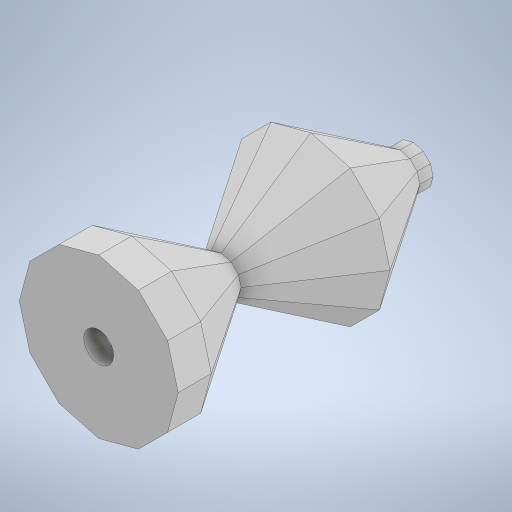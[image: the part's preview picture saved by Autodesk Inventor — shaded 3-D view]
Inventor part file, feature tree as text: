
AUTODESK INVENTOR PART (.ipt)
format: ipt  version: 2023 (Build 270158000, 158)  size: 357,376 bytes
history: native  units: in
note: dims shown in document units (in); Inventor stores cm internally (conversion verified against a paired STEP export)
features: sketch x7, extrude x4, projected_geometry x3, other x2, mirror x2, loft x1, shell x1
ambient origin geometry x8: Origin, YZ Plane, XZ Plane, XY Plane, X Axis, Y Axis, Z Axis, Center Point
bodies: Body1 (feature_tree)
feature tree (20):
  other  "솔리드1"
  sketch  "스케치1"
  other  "작업 평면1"
  loft  "로프트1"
  mirror  "미러1"
  mirror  "미러2"
  extrude  "돌출5"  Depth=0.5315in
  shell  "쉘2"  Thickness=0.2362in
  extrude  "돌출6"  TaperAngle=0.0deg  [1 undecoded]
  sketch  "스케치9"
  sketch  "스케치10"
  extrude  "돌출7"  TaperAngle=0.0deg  [1 undecoded]
  extrude  "돌출8"  Depth=0.0984in TaperAngle=0.0deg
  sketch  "스케치2"
  sketch  "스케치7"
  projected_geometry  "투영된 루프4"
  sketch  "스케치8"
  projected_geometry  "투영된 루프5"
  sketch  "스케치11"
  projected_geometry  "투영된 루프6"
note: 2 required parameter values undecoded (feature->parameter linkage not recoverable at this tier; creation-order binding heuristic only, values carry confidence <= 0.55)
